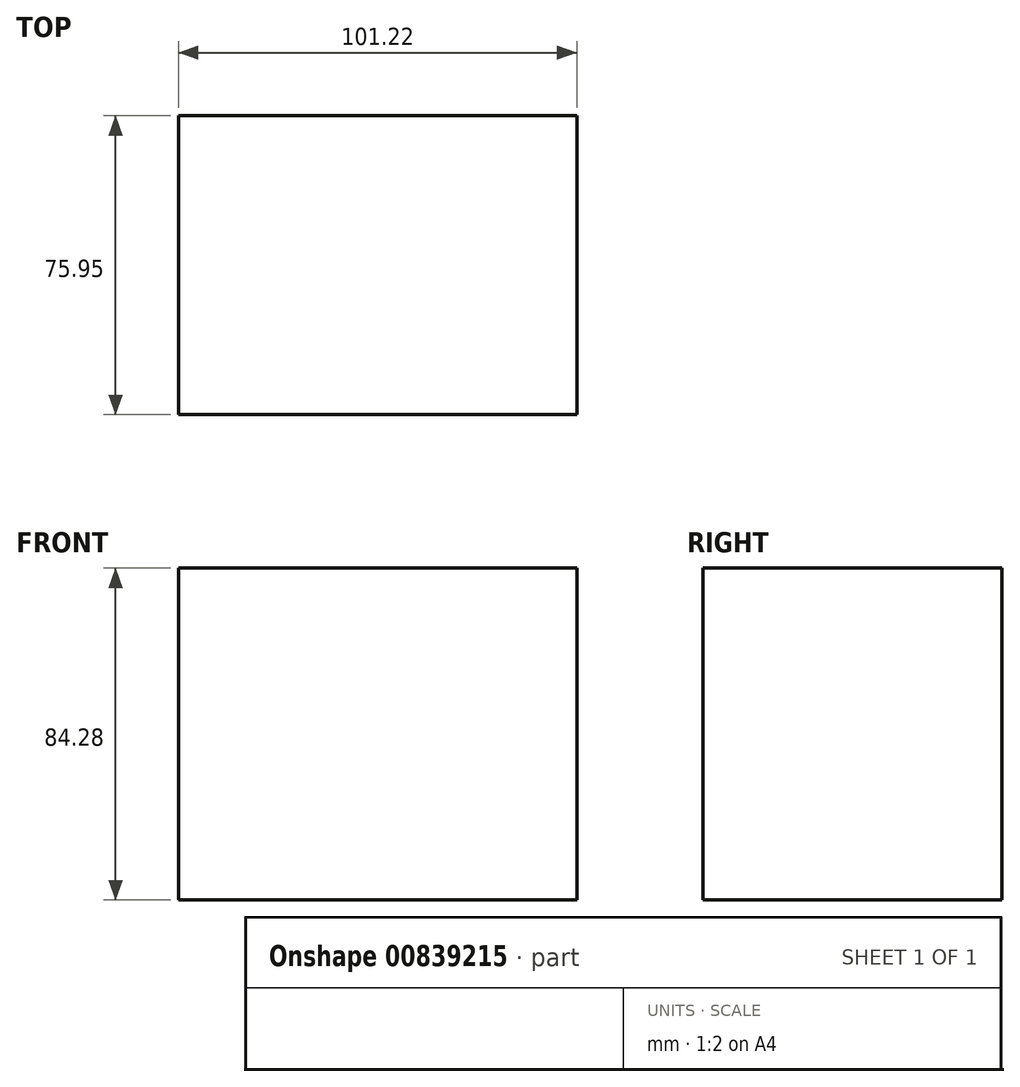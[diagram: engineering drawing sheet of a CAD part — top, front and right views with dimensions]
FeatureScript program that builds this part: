
annotation { "Feature Type Name" : "Feature", "Feature Type Description" : "" }
export const myFeature = defineFeature(function(context is Context, id is Id, definition is map)
    precondition{}
    {
        {
            var Q0;
            Q0=qCreatedBy(makeId("Front.planeOp"),FACE);
            var sketch = newSketch(context, id + "F0", { "sketchPlane" : qUnion([Q0])});
            skLineSegment(sketch, "E0", {"start": v(-53.94, 43.73) * mm, "end": v(-53.94, -40.55) * mm});
            skLineSegment(sketch, "E1", {"start": v(-53.94, -40.55) * mm, "end": v(47.28, -40.55) * mm});
            skLineSegment(sketch, "E2", {"start": v(47.28, -40.55) * mm, "end": v(47.28, 43.73) * mm});
            skLineSegment(sketch, "E3", {"start": v(-53.94, 43.73) * mm, "end": v(47.28, 43.73) * mm});
            skSolve(sketch);
        }
        {
            var Q0;
            Q0=makeQuery(id+"F0.imprint","IMPRINT",FACE,{"disambiguationData":[TD([[makeQuery(id+"F0.imprint","IMPRINT",EDGE,{"derivedFrom":sQuery(id+"F0.wireOp",EDGE,"E0")}),1.0]])]});
            extrude(context, id + "F1", {"entities" : qUnion([Q0]), "depth" : 75.95 * mm, "offsetDistance" : 25.4 * mm});
        }
    });
